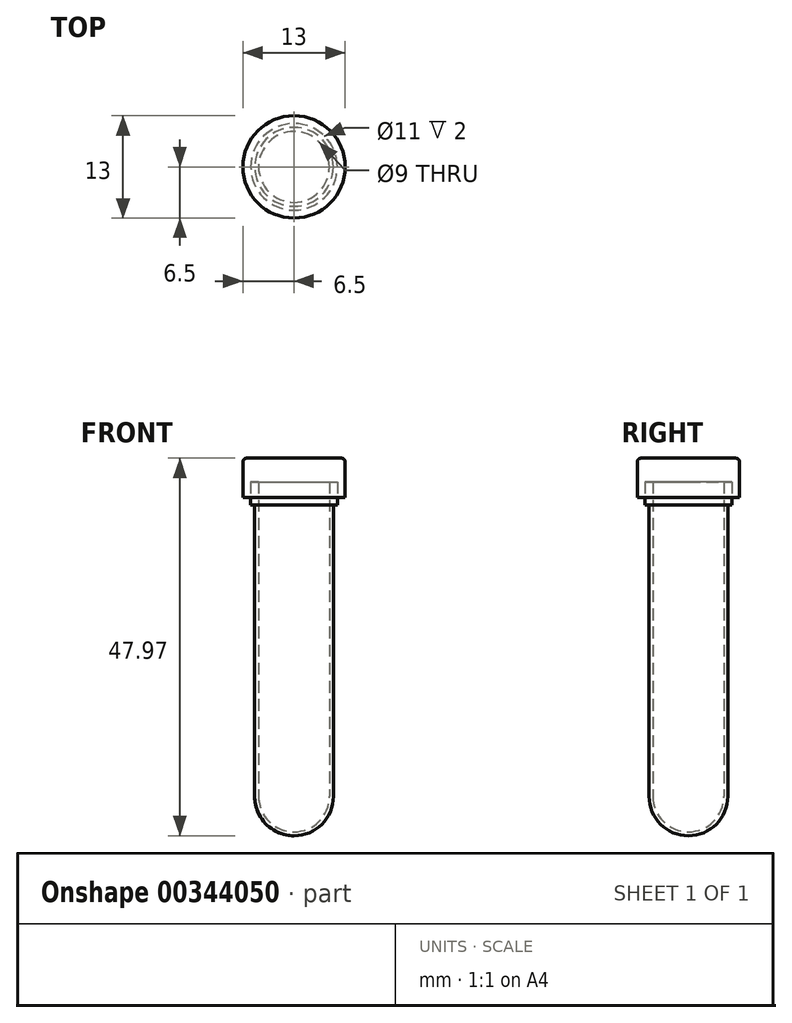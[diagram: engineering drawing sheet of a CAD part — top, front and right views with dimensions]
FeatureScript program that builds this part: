
annotation { "Feature Type Name" : "Feature", "Feature Type Description" : "" }
export const myFeature = defineFeature(function(context is Context, id is Id, definition is map)
    precondition{}
    {
        {
            var Q0;
            Q0=qCreatedBy(makeId("Front.planeOp"),FACE);
            var sketch = newSketch(context, id + "F0", { "sketchPlane" : qUnion([Q0])});
            skLineSegment(sketch, "E0", {"start": v(-5, -0.47) * mm, "end": v(-5, -37.47) * mm});
            skLineSegment(sketch, "E1", {"start": v(0, -42.47) * mm, "end": v(0, -42.47) * mm});
            skLineSegment(sketch, "E2.0", {"start": v(-4.5, 2.5) * mm, "end": v(-4.5, -37.47) * mm});
            skPoint(sketch, "E3.visualSharp", {"position": v(-4.5, -41.97) * mm});
            skArc(sketch, "E3.filletArc", {"start": v(-4.5, -37.47) * mm, "mid": v(-3.18, -40.65) * mm, "end": v(0, -41.97) * mm});
            skPoint(sketch, "E4.visualSharp", {"position": v(-5, -42.47) * mm});
            skArc(sketch, "E4.filletArc", {"start": v(-5, -37.47) * mm, "mid": v(-3.54, -41) * mm, "end": v(0, -42.47) * mm});
            skLineSegment(sketch, "E5", {"start": v(-5.5, 2.5) * mm, "end": v(-5.5, 0) * mm});
            skPoint(sketch, "E6.orphan", {"position": v(-5, 2.53) * mm});
            skLineSegment(sketch, "E7", {"start": v(-5, -0.47) * mm, "end": v(-5.5, -0.47) * mm});
            skLineSegment(sketch, "E8", {"start": v(-5.5, -0.47) * mm, "end": v(-5.5, 0) * mm});
            skPoint(sketch, "E9.orphan", {"position": v(-6.43, 2.5) * mm});
            skLineSegment(sketch, "E10", {"start": v(0, -41.97) * mm, "end": v(0, -42.47) * mm});
            skLineSegment(sketch, "E11", {"start": v(0, -46.13) * mm, "end": v(0, 19.61) * mm, "construction": true});
            skLineSegment(sketch, "E12", {"start": v(-5.5, 2.5) * mm, "end": v(-4.5, 2.5) * mm});
            skPoint(sketch, "E13.orphan", {"position": v(1.52, 2.53) * mm});
            skSolve(sketch);
        }
        {
            var Q0;
            Q0=qSketchRegion(id+"F0",true);
            var Q1;
            Q1=sQuery(id+"F0.wireOp",EDGE,"E11");
            revolve(context, id + "F1", {"entities" : qUnion([Q0]), "axis" : qUnion([Q1]), "revolveType" : RevolveType.FULL});
        }
        {
            var Q0;
            Q0=qCreatedBy(makeId("Front.planeOp"),FACE);
            var sketch = newSketch(context, id + "F2", { "sketchPlane" : qUnion([Q0])});
            skLineSegment(sketch, "E14", {"start": v(0, 5.5) * mm, "end": v(-6.5, 5.5) * mm});
            skLineSegment(sketch, "E15", {"start": v(-6.5, 5.5) * mm, "end": v(-6.5, 0.5) * mm});
            skLineSegment(sketch, "E16", {"start": v(-6.5, 0.5) * mm, "end": v(-5.5, 0.5) * mm});
            skLineSegment(sketch, "E17", {"start": v(-5.5, 0.5) * mm, "end": v(-5.5, 2.5) * mm});
            skLineSegment(sketch, "E18", {"start": v(-5.5, 2.5) * mm, "end": v(0, 2.5) * mm});
            skLineSegment(sketch, "E19", {"start": v(0, 2.5) * mm, "end": v(0, 5.5) * mm});
            skLineSegment(sketch, "E20", {"start": v(0, 0) * mm, "end": v(0, 4.2) * mm, "construction": true});
            skLineSegment(sketch, "E21", {"start": v(0, 5.5) * mm, "end": v(0, 2.5) * mm});
            skSolve(sketch);
        }
        {
            var Q0;
            Q0=makeQuery(id+"F2.imprint","IMPRINT",FACE,{"disambiguationData":[TD([[makeQuery(id+"F2.imprint","IMPRINT",EDGE,{"derivedFrom":sQuery(id+"F2.wireOp",EDGE,"E14")}),1.0]])]});
            var Q1;
            Q1=sQuery(id+"F2.wireOp",EDGE,"E20");
            revolve(context, id + "F3", {"entities" : qUnion([Q0]), "axis" : qUnion([Q1]), "revolveType" : RevolveType.FULL});
        }
        {
            var Q0;
            Q0=makeQuery(id+"F3.opRevolve","SWEPT_EDGE",EDGE,{"disambiguationData":[OSD([sQuery(id+"F2.wireOp",EDGE,"E14"),sQuery(id+"F2.wireOp",EDGE,"E15")])]});
            fillet(context, id + "F4", {"entities" : qUnion([Q0]), "radius" : 0.5 * mm, "tangentPropagation" : true, "allowEdgeOverflow" : false});
        }
    });
